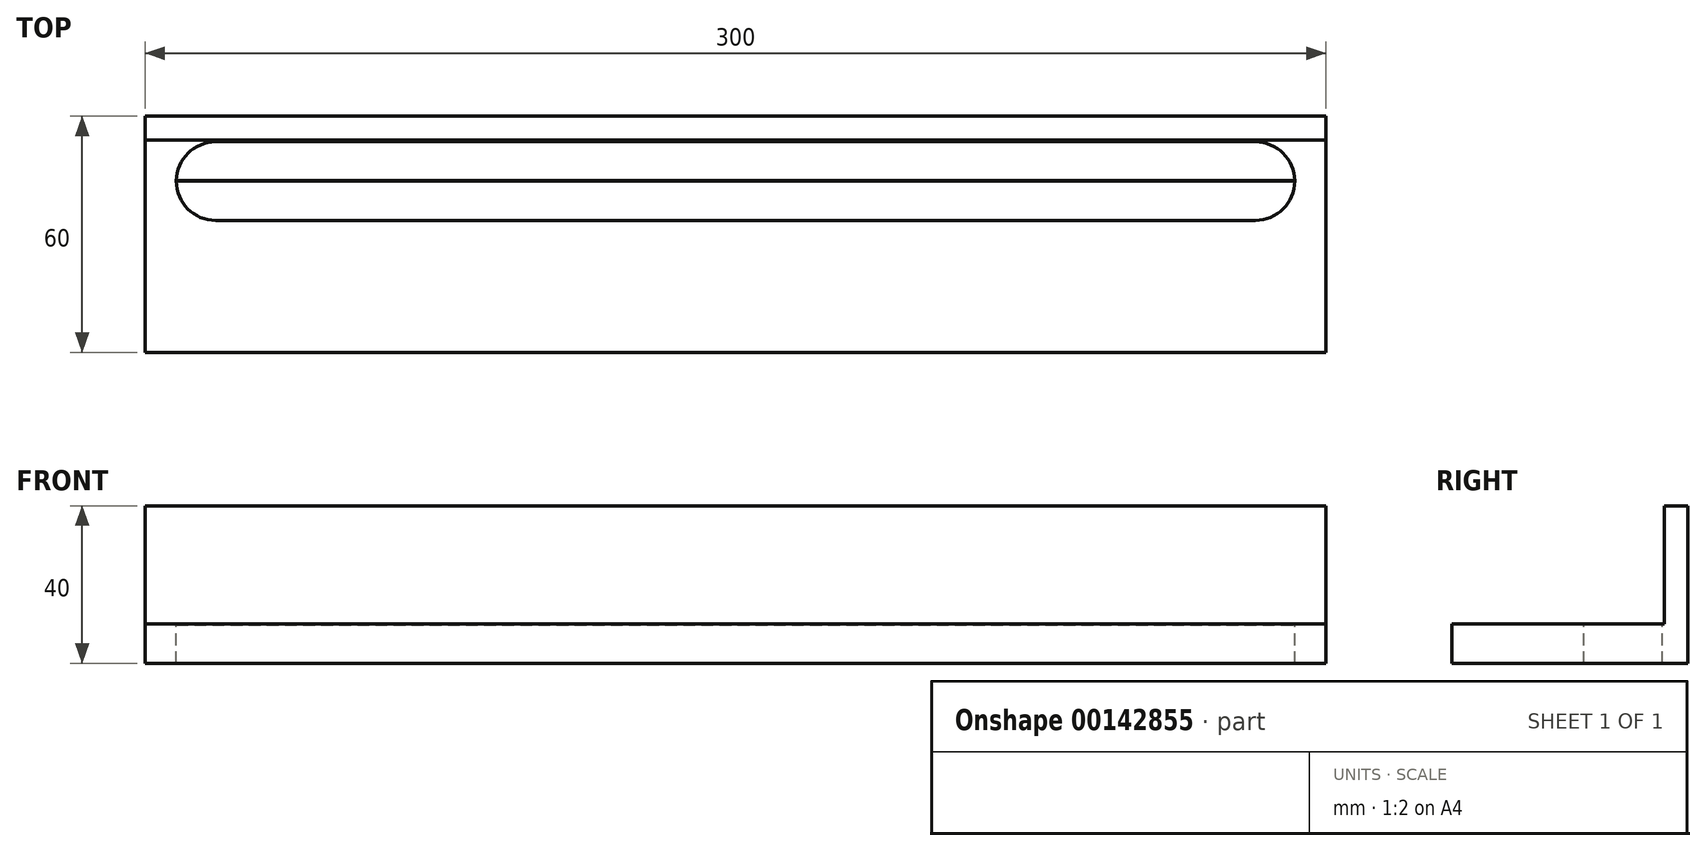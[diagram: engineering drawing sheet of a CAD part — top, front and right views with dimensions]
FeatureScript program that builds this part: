
annotation { "Feature Type Name" : "Feature", "Feature Type Description" : "" }
export const myFeature = defineFeature(function(context is Context, id is Id, definition is map)
    precondition{}
    {
        {
            var Q0;
            Q0=qCreatedBy(makeId("Right.planeOp"),FACE);
            var sketch = newSketch(context, id + "F0", { "sketchPlane" : qUnion([Q0])});
            skLineSegment(sketch, "E0", {"start": v(0, 0) * mm, "end": v(-60, 0) * mm});
            skLineSegment(sketch, "E1", {"start": v(-60, 0) * mm, "end": v(-60, 10) * mm});
            skLineSegment(sketch, "E2", {"start": v(-60, 10) * mm, "end": v(-6, 10) * mm});
            skLineSegment(sketch, "E3", {"start": v(-6, 10) * mm, "end": v(-6, 40) * mm});
            skLineSegment(sketch, "E4", {"start": v(-6, 40) * mm, "end": v(0, 40) * mm});
            skLineSegment(sketch, "E5", {"start": v(0, 40) * mm, "end": v(0, 0) * mm});
            skSolve(sketch);
        }
        {
            var Q0;
            Q0 = qSketchRegion(id + "F0", true);
            extrude(context, id + "F1", {"entities" : qUnion([Q0]), "depth" : 300 * mm});
        }
        {
            var Q0;
            Q0=makeQuery(id+"F1.opExtrude","SWEPT_FACE",FACE,{"disambiguationData":[OSD([sQuery(id+"F0.wireOp",EDGE,"E2")])]});
            var sketch = newSketch(context, id + "F2", { "sketchPlane" : qUnion([Q0])});
            skLineSegment(sketch, "E6", {"start": v(150, -60) * mm, "end": v(150, -6) * mm, "construction": true});
            skArc(sketch, "E7", {"start": v(17.94, -6.5) * mm, "mid": v(7.94, -16.5) * mm, "end": v(17.94, -26.5) * mm});
            skLineSegment(sketch, "E8", {"start": v(17.94, -26.5) * mm, "end": v(150, -26.5) * mm});
            skLineSegment(sketch, "E9", {"start": v(17.94, -6.5) * mm, "end": v(150, -6.5) * mm});
            skLineSegment(sketch, "E10.MirrorCS", {"start": v(282.06, -26.5) * mm, "end": v(150, -26.5) * mm});
            skArc(sketch, "E11.MirrorCS", {"start": v(282.06, -6.5) * mm, "mid": v(292.06, -16.5) * mm, "end": v(282.06, -26.5) * mm});
            skLineSegment(sketch, "E12.MirrorCS", {"start": v(282.06, -6.5) * mm, "end": v(150, -6.5) * mm});
            skLineSegment(sketch, "E13", {"start": v(0, -16.5) * mm, "end": v(300, -16.5) * mm, "construction": true});
            skSolve(sketch);
        }
        {
            var Q0;
            Q0 = qSketchRegion(id + "F2", true);
            extrude(context, id + "F3", {"entities" : qUnion([Q0]), "operationType" : NewBodyOperationType.REMOVE, "endBound" : BoundingType.THROUGH_ALL, "oppositeDirection" : true, "depth" : 25 * mm});
        }
        {
            var Q0;
            Q0=makeQuery(id+"F1.opExtrude","SWEPT_FACE",FACE,{"disambiguationData":[OSD([sQuery(id+"F0.wireOp",EDGE,"E2")])]});
            var sketch = newSketch(context, id + "F4", { "sketchPlane" : qUnion([Q0])});
            skLineSegment(sketch, "E14", {"start": v(7.94, -16.5) * mm, "end": v(292.06, -16.5) * mm});
            skLineSegment(sketch, "E15.0", {"start": v(7.94, -16.4) * mm, "end": v(292.06, -16.4) * mm});
            skLineSegment(sketch, "E16", {"start": v(292.06, -16.4) * mm, "end": v(292.06, -16.5) * mm});
            skLineSegment(sketch, "E17", {"start": v(7.94, -16.4) * mm, "end": v(7.94, -16.5) * mm});
            skLineSegment(sketch, "E18", {"start": v(15.44, -20) * mm, "end": v(15.44, -17.7) * mm});
            skSolve(sketch);
        }
        {
            var Q0;
            Q0 = qSketchRegion(id + "F4", true);
            extrude(context, id + "F5", {"entities" : qUnion([Q0]), "operationType" : NewBodyOperationType.ADD, "oppositeDirection" : true, "depth" : .2 * mm});
        }
    });
